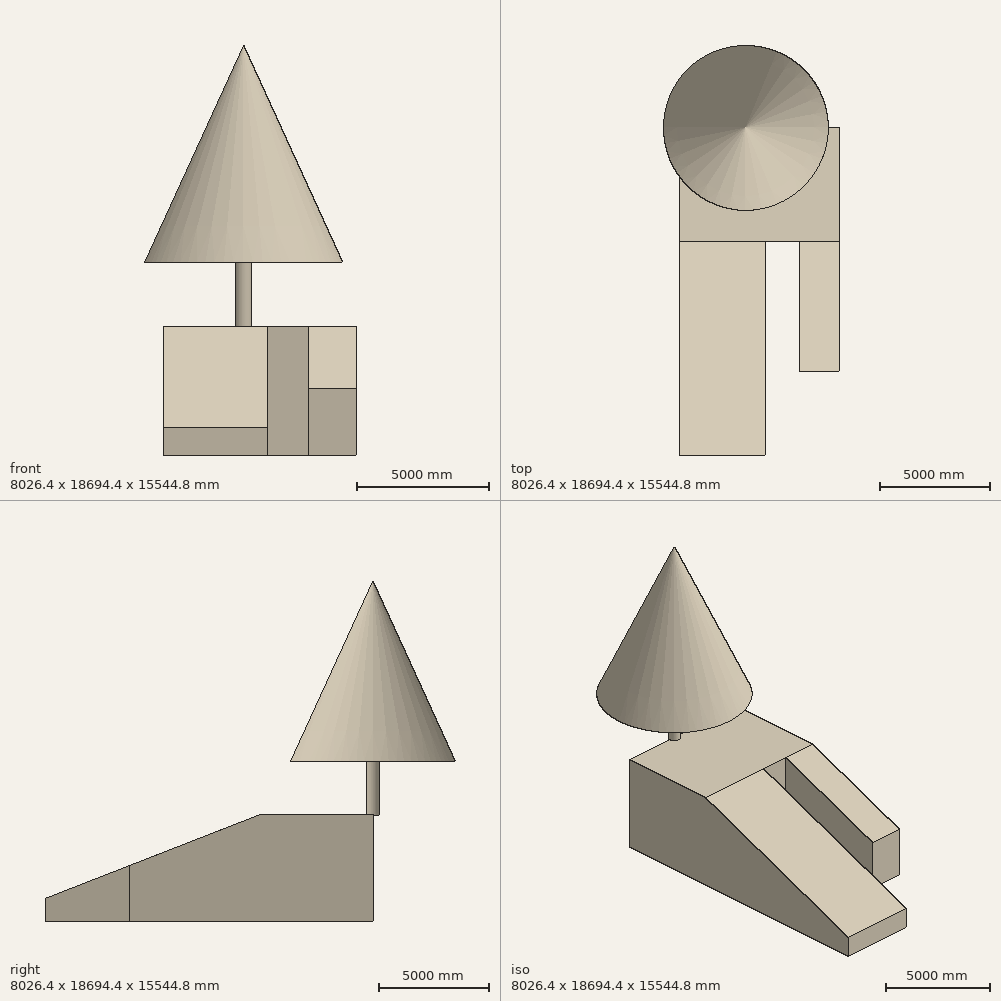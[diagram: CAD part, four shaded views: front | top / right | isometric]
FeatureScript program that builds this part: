
annotation { "Feature Type Name" : "Feature", "Feature Type Description" : "" }
export const myFeature = defineFeature(function(context is Context, id is Id, definition is map)
    precondition{}
    {
        {
            var Q0;
            Q0=qCreatedBy(makeId("Front.planeOp"),FACE);
            var sketch = newSketch(context, id + "F0", { "sketchPlane" : qUnion([Q0])});
            skLineSegment(sketch, "E0", {"start": v(0, 0) * mm, "end": v(304.8, 0) * mm});
            skLineSegment(sketch, "E1", {"start": v(304.8, 0) * mm, "end": v(304.8, 2438.4) * mm});
            skLineSegment(sketch, "E2", {"start": v(304.8, 2438.4) * mm, "end": v(3759.2, 2438.4) * mm});
            skLineSegment(sketch, "E3", {"start": v(3759.2, 2438.4) * mm, "end": v(0, 10668) * mm});
            skLineSegment(sketch, "E4", {"start": v(0, 10668) * mm, "end": v(0, 0) * mm});
            skSolve(sketch);
        }
        {
            var Q0;
            Q0=qCreatedBy(makeId("Front.planeOp"),FACE);
            var sketch = newSketch(context, id + "F1", { "sketchPlane" : qUnion([Q0])});
            skLineSegment(sketch, "E5", {"start": v(0, 0) * mm, "end": v(0, -952.81) * mm, "construction": true});
            skSolve(sketch);
        }
        {
            var Q0;
            Q0 = qSketchRegion(id + "F0", true);
            var Q1;
            Q1=sQuery(id+"F1.wireOp",EDGE,"E5");
            revolve(context, id + "F2", {"entities" : qUnion([Q0]), "axis" : qUnion([Q1]), "revolveType" : RevolveType.FULL});
        }
        {
            var Q0;
            Q0=qCreatedBy(makeId("Front.planeOp"),FACE);
            var sketch = newSketch(context, id + "F3", { "sketchPlane" : qUnion([Q0])});
            skLineSegment(sketch, "E6.bottom", {"start": v(-3048, 0) * mm, "end": v(4267.2, 0) * mm});
            skLineSegment(sketch, "E6.top", {"start": v(-3048, -4876.8) * mm, "end": v(4267.2, -4876.8) * mm});
            skLineSegment(sketch, "E6.left", {"start": v(-3048, 0) * mm, "end": v(-3048, -4876.8) * mm});
            skLineSegment(sketch, "E6.right", {"start": v(4267.2, 0) * mm, "end": v(4267.2, -4876.8) * mm});
            skSolve(sketch);
        }
        {
            var Q0;
            Q0 = qSketchRegion(id + "F3", true);
            extrude(context, id + "F4", {"entities" : qUnion([Q0]), "depth" : 5181.6 * mm});
        }
        {
            var Q0;
            Q0=makeQuery(id+"F4.opExtrude","SWEPT_FACE",FACE,{"disambiguationData":[OSD([sQuery(id+"F3.wireOp",EDGE,"E6.right")])]});
            var sketch = newSketch(context, id + "F5", { "sketchPlane" : qUnion([Q0])});
            skLineSegment(sketch, "E7", {"start": v(-5181.6, -4876.8) * mm, "end": v(-5181.6, 0) * mm});
            skLineSegment(sketch, "E8", {"start": v(-5181.6, 0) * mm, "end": v(-14935.2, -3810) * mm});
            skLineSegment(sketch, "E9", {"start": v(-14935.2, -3810) * mm, "end": v(-14935.2, -4876.8) * mm});
            skLineSegment(sketch, "E10", {"start": v(-14935.2, -4876.8) * mm, "end": v(-5181.6, -4876.8) * mm});
            skSolve(sketch);
        }
        {
            var Q0;
            Q0 = qSketchRegion(id + "F5", true);
            var Q1;
            Q1=makeQuery(id+"F4.opExtrude","SWEPT_FACE",FACE,{"disambiguationData":[OSD([sQuery(id+"F3.wireOp",EDGE,"E6.left")])]});
            extrude(context, id + "F6", {"entities" : qUnion([Q0]), "operationType" : NewBodyOperationType.ADD, "endBound" : BoundingType.UP_TO_SURFACE, "oppositeDirection" : true, "endBoundEntityFace" : qUnion([Q1]), "depth" : 25.4 * mm});
        }
        {
            var Q0;
            Q0=makeQuery(id+"F6.boolean.opBoolean","MERGE",FACE,{"derivedFrom":[makeQuery(id+"F4.opExtrude","SWEPT_FACE",FACE,{"disambiguationData":[OSD([sQuery(id+"F3.wireOp",EDGE,"E6.right")])]}),makeQuery(id+"F6.opExtrude","CAP_FACE",FACE,{"disambiguationData":[OSD([sQuery(id+"F5.wireOp",EDGE,"E7"),sQuery(id+"F5.wireOp",EDGE,"E8"),sQuery(id+"F5.wireOp",EDGE,"E9"),sQuery(id+"F5.wireOp",EDGE,"E10")])],"isStart":true})]});
            cPlane(context, id + "F7", {"entities" : qUnion([Q0]), "cplaneType" : CPlaneType.OFFSET, "offset" : 1828.8 * mm, "oppositeDirection" : true, "width" : 152.4 * mm, "height" : 152.4 * mm});
        }
        {
            var Q0;
            Q0=qCreatedBy(id+"F7.planeOp",FACE);
            var sketch = newSketch(context, id + "F8", { "sketchPlane" : qUnion([Q0])});
            skLineSegment(sketch, "E11.bottom", {"start": v(-5181.6, 0) * mm, "end": v(-14935.2, 0) * mm});
            skLineSegment(sketch, "E11.top", {"start": v(-5181.6, -4876.8) * mm, "end": v(-14935.2, -4876.8) * mm});
            skLineSegment(sketch, "E11.left", {"start": v(-5181.6, 0) * mm, "end": v(-5181.6, -4876.8) * mm});
            skLineSegment(sketch, "E11.right", {"start": v(-14935.2, 0) * mm, "end": v(-14935.2, -4876.8) * mm});
            skSolve(sketch);
        }
        {
            var Q0;
            Q0 = qSketchRegion(id + "F8", true);
            extrude(context, id + "F9", {"entities" : qUnion([Q0]), "operationType" : NewBodyOperationType.REMOVE, "oppositeDirection" : true, "depth" : 1524 * mm});
        }
        {
            var Q0;
            Q0=makeQuery(id+"F6.boolean.opBoolean","MERGE",FACE,{"derivedFrom":[makeQuery(id+"F4.opExtrude","SWEPT_FACE",FACE,{"disambiguationData":[OSD([sQuery(id+"F3.wireOp",EDGE,"E6.right")])]}),makeQuery(id+"F6.opExtrude","CAP_FACE",FACE,{"disambiguationData":[OSD([sQuery(id+"F5.wireOp",EDGE,"E7"),sQuery(id+"F5.wireOp",EDGE,"E8"),sQuery(id+"F5.wireOp",EDGE,"E9"),sQuery(id+"F5.wireOp",EDGE,"E10")])],"isStart":true})]});
            var sketch = newSketch(context, id + "F10", { "sketchPlane" : qUnion([Q0])});
            skLineSegment(sketch, "E12", {"start": v(-14935.2, -4876.8) * mm, "end": v(-11125.2, -4876.8) * mm});
            skLineSegment(sketch, "E13", {"start": v(-11125.2, -4876.8) * mm, "end": v(-11125.2, -2321.72) * mm});
            skLineSegment(sketch, "E14", {"start": v(-11125.2, -2321.72) * mm, "end": v(-14935.2, -3810) * mm});
            skLineSegment(sketch, "E15", {"start": v(-14935.2, -3810) * mm, "end": v(-14935.2, -4876.8) * mm});
            skSolve(sketch);
        }
        {
            var Q0;
            Q0=makeQuery(id+"F10.imprint","IMPRINT",FACE,{"disambiguationData":[TD([[makeQuery(id+"F10.imprint","IMPRINT",EDGE,{"derivedFrom":sQuery(id+"F10.wireOp",EDGE,"E12")}),1.0]])]});
            var Q1;
            Q1=makeQuery(id+"F9.boolean.opBoolean","COPY",FACE,{"derivedFrom":makeQuery(id+"F9.opExtrude","CAP_FACE",FACE,{"disambiguationData":[OSD([sQuery(id+"F8.wireOp",EDGE,"E11.bottom"),sQuery(id+"F8.wireOp",EDGE,"E11.top"),sQuery(id+"F8.wireOp",EDGE,"E11.left"),sQuery(id+"F8.wireOp",EDGE,"E11.right")])],"isStart":false})});
            extrude(context, id + "F11", {"entities" : qUnion([Q0]), "operationType" : NewBodyOperationType.REMOVE, "endBound" : BoundingType.UP_TO_SURFACE, "oppositeDirection" : true, "endBoundEntityFace" : qUnion([Q1]), "depth" : 25.4 * mm});
        }
    });
